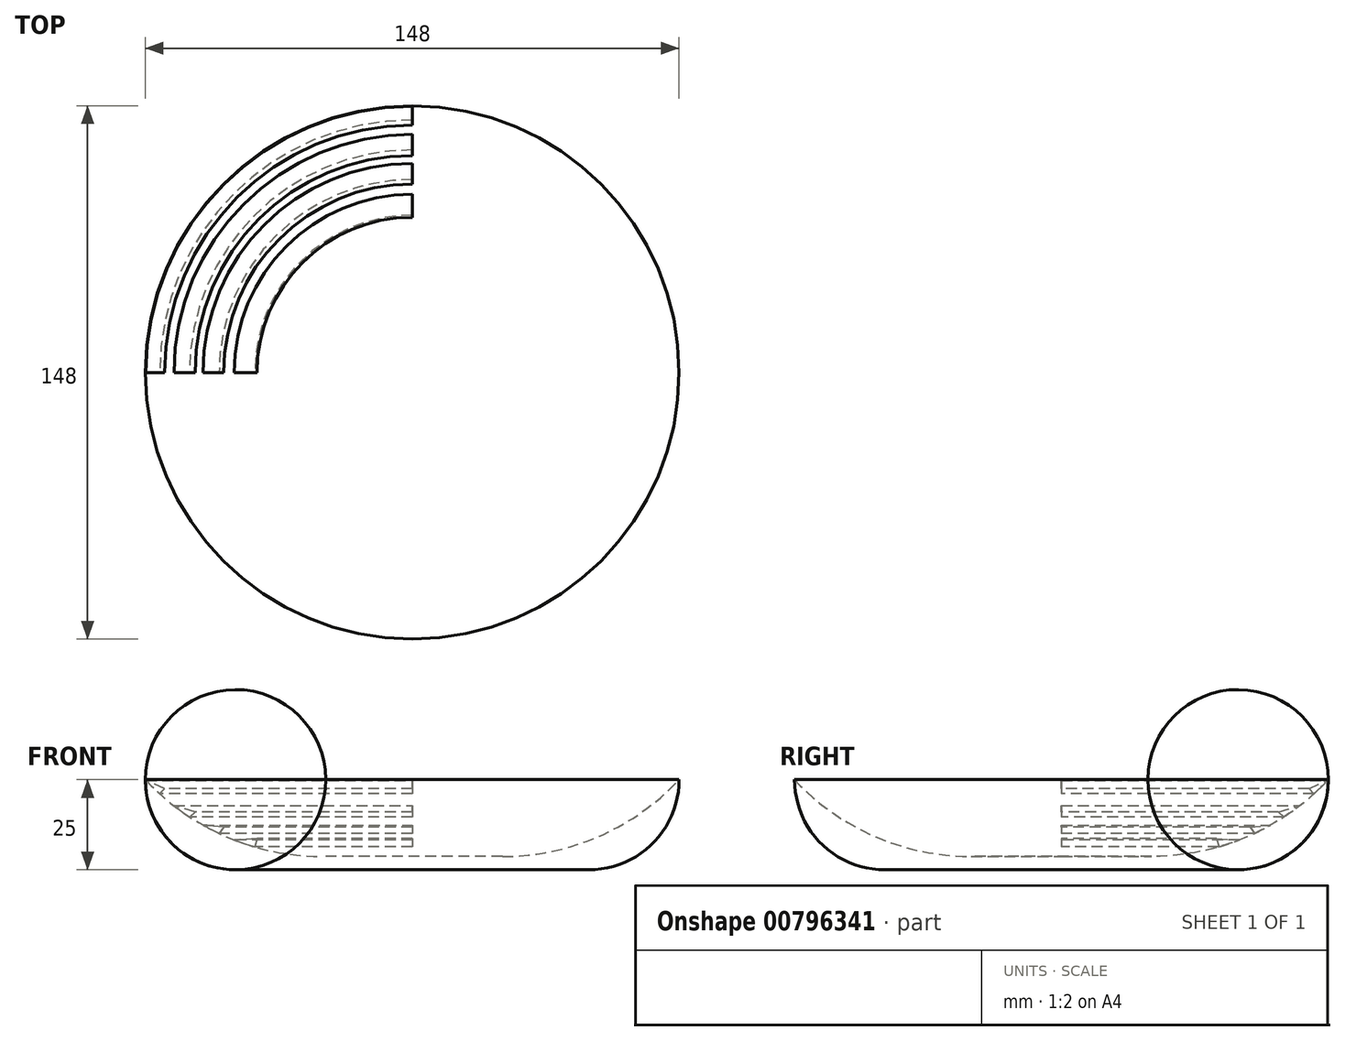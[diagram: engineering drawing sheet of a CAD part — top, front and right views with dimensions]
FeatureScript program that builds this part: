
annotation { "Feature Type Name" : "Feature", "Feature Type Description" : "" }
export const myFeature = defineFeature(function(context is Context, id is Id, definition is map)
    precondition{}
    {
        {
            var Q0;
            Q0=qCreatedBy(makeId("Front.planeOp"),FACE);
            var sketch = newSketch(context, id + "F0", { "sketchPlane" : qUnion([Q0])});
            skLineSegment(sketch, "E0", {"start": v(0, 0) * mm, "end": v(-25, 0) * mm});
            skArc(sketch, "E1", {"start": v(-74, 21.3) * mm, "mid": v(-51.72, 5.56) * mm, "end": v(-25, 0) * mm});
            skLineSegment(sketch, "E2", {"start": v(0, 0) * mm, "end": v(0, -3.7) * mm});
            skLineSegment(sketch, "E3", {"start": v(0, -3.7) * mm, "end": v(-74, -3.7) * mm});
            skLineSegment(sketch, "E4", {"start": v(-74, -3.7) * mm, "end": v(-74, 21.3) * mm});
            skSolve(sketch);
        }
        {
            var Q0;
            Q0 = qSketchRegion(id + "F0", true);
            var Q1;
            Q1=sQuery(id+"F0.wireOp",EDGE,"E2");
            revolve(context, id + "F1", {"surfaceOperationType" : NewSurfaceOperationType.NEW, "entities" : qUnion([Q0]), "axis" : qUnion([Q1]), "revolveType" : RevolveType.FULL});
        }
        {
            var Q0;
            Q0=makeQuery(id+"F1.opRevolve","SWEPT_EDGE",EDGE,{"disambiguationData":[OSD([sQuery(id+"F0.wireOp",EDGE,"E3"),sQuery(id+"F0.wireOp",EDGE,"E4")])]});
            fillet(context, id + "F2", {"entities" : qUnion([Q0]), "radius" : 25 * mm, "tangentPropagation" : true, "allowEdgeOverflow" : false});
        }
        {
            var Q0;
            Q0=qCreatedBy(makeId("Front.planeOp"),FACE);
            var sketch = newSketch(context, id + "F3", { "sketchPlane" : qUnion([Q0])});
            skArc(sketch, "E5", {"start": v(-74, 21.21) * mm, "mid": v(-51.7, 5.53) * mm, "end": v(-25, 0) * mm});
            skLineSegment(sketch, "E6", {"start": v(-68.66, 18.85) * mm, "end": v(-74, 21.21) * mm});
            skLineSegment(sketch, "E7", {"start": v(-60.2, 12.36) * mm, "end": v(-66.17, 14.09) * mm});
            skLineSegment(sketch, "E8", {"start": v(-52.27, 8.2) * mm, "end": v(-58.06, 8.7) * mm});
            skLineSegment(sketch, "E9", {"start": v(-43.06, 4.93) * mm, "end": v(-49.45, 4.6) * mm});
            skLineSegment(sketch, "E10", {"start": v(-68.66, 18.85) * mm, "end": v(-70.06, 17.35) * mm});
            skLineSegment(sketch, "E11", {"start": v(-60.2, 12.36) * mm, "end": v(-61.77, 10.96) * mm});
            skLineSegment(sketch, "E12", {"start": v(-52.27, 8.2) * mm, "end": v(-53.55, 6.37) * mm});
            skLineSegment(sketch, "E13", {"start": v(-43.06, 4.93) * mm, "end": v(-43.63, 2.64) * mm});
            skLineSegment(sketch, "E14", {"start": v(-43.63, 2.64) * mm, "end": v(-49.45, 4.6) * mm});
            skLineSegment(sketch, "E15", {"start": v(-53.55, 6.37) * mm, "end": v(-58.06, 8.7) * mm});
            skLineSegment(sketch, "E16", {"start": v(-61.77, 10.96) * mm, "end": v(-66.17, 14.09) * mm});
            skLineSegment(sketch, "E17", {"start": v(-70.06, 17.35) * mm, "end": v(-74, 21.21) * mm});
            skLineSegment(sketch, "E18", {"start": v(0, 0) * mm, "end": v(0, -2.2) * mm});
            skSolve(sketch);
        }
        {
            var Q0;
            Q0 = qSketchRegion(id + "F3", true);
            var Q1;
            Q1=sQuery(id+"F3.wireOp",EDGE,"E18");
            revolve(context, id + "F4", {"operationType" : NewBodyOperationType.ADD, "surfaceOperationType" : NewSurfaceOperationType.NEW, "entities" : qUnion([Q0]), "axis" : qUnion([Q1]), "revolveType" : RevolveType.ONE_DIRECTION, "angle" : 90 * degree});
        }
    });
